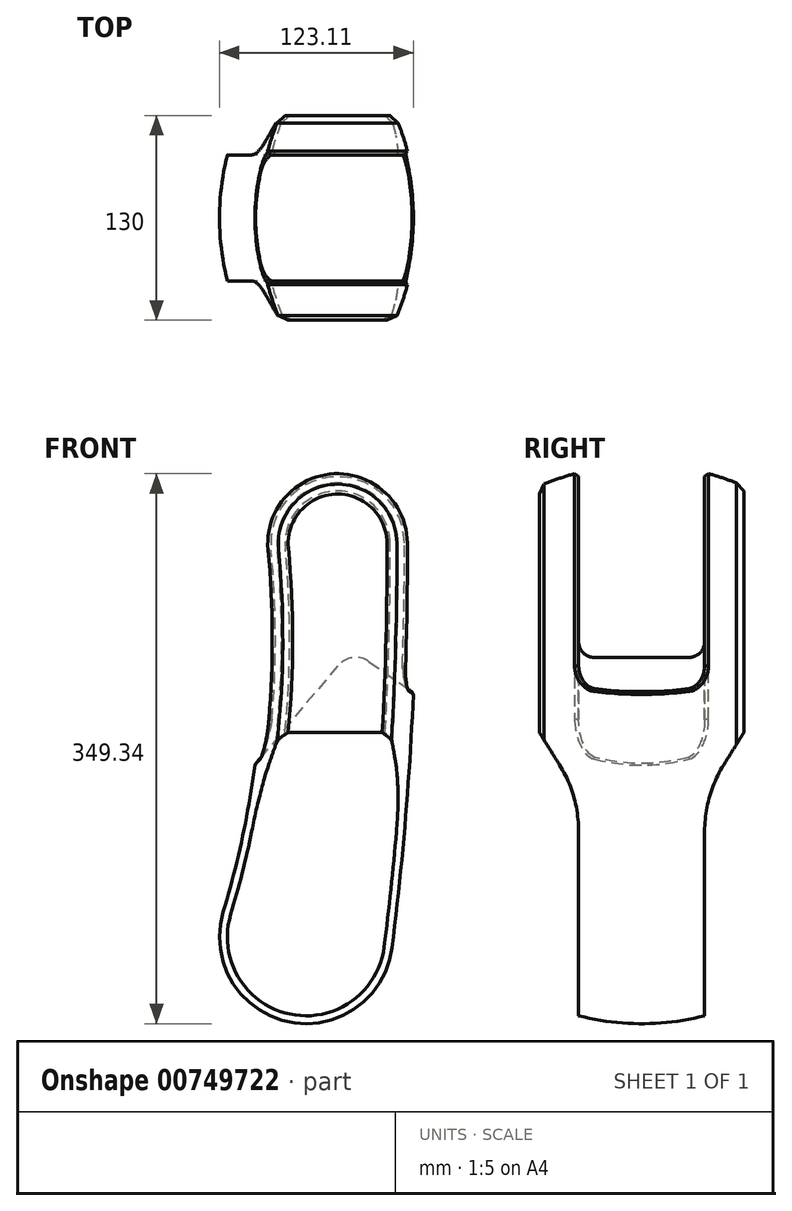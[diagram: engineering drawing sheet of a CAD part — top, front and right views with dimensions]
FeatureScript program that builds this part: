
annotation { "Feature Type Name" : "Feature", "Feature Type Description" : "" }
export const myFeature = defineFeature(function(context is Context, id is Id, definition is map)
    precondition{}
    {
        {
            var Q0;
            Q0=qCreatedBy(makeId("Front.planeOp"),FACE);
            var sketch = newSketch(context, id + "F0", { "sketchPlane" : qUnion([Q0])});
            skArc(sketch, "E0", {"start": v(50, 0.22) * mm, "mid": v(-2.46, 49.94) * mm, "end": v(-49.78, -4.7) * mm});
            skLineSegment(sketch, "E1", {"start": v(0, 0) * mm, "end": v(0, -250) * mm, "construction": true});
            skLineSegment(sketch, "E2", {"start": v(0, -250) * mm, "end": v(-20, -250) * mm, "construction": true});
            skArc(sketch, "E3", {"start": v(-72.66, -234.13) * mm, "mid": v(-31.39, -303.8) * mm, "end": v(34.58, -256.82) * mm});
            skArc(sketch, "E4", {"start": v(-72.66, -234.13) * mm, "mid": v(-50.1, -120.52) * mm, "end": v(-49.78, -4.7) * mm});
            skArc(sketch, "E5", {"start": v(34.58, -256.82) * mm, "mid": v(46.43, -128.55) * mm, "end": v(50, 0.22) * mm});
            skSolve(sketch);
        }
        {
            var Q0;
            Q0=qSketchRegion(id+"F0",true);
            extrude(context, id + "F1", {"entities" : qUnion([Q0]), "endBound" : BoundingType.SYMMETRIC, "depth" : 130 * mm, "offsetDistance" : 25 * mm});
        }
        {
            var Q0;
            Q0=qCreatedBy(makeId("Right.planeOp"),FACE);
            var sketch = newSketch(context, id + "F2", { "sketchPlane" : qUnion([Q0])});
            skLineSegment(sketch, "E6", {"start": v(0, 0) * mm, "end": v(0, -81.12) * mm, "construction": true});
            skLineSegment(sketch, "E7", {"start": v(0, 0) * mm, "end": v(0, 50) * mm, "construction": true});
            skArc(sketch, "E8", {"start": v(70, 34.15) * mm, "mid": v(0, 50) * mm, "end": v(-70, 34.15) * mm});
            skLineSegment(sketch, "E9", {"start": v(0, 50) * mm, "end": v(0, 72.15) * mm, "construction": true});
            skLineSegment(sketch, "E10", {"start": v(0, 72.15) * mm, "end": v(-70, 72.15) * mm});
            skLineSegment(sketch, "E11", {"start": v(-70, 72.15) * mm, "end": v(-70, 34.15) * mm});
            skLineSegment(sketch, "E12", {"start": v(-40, 72.15) * mm, "end": v(-40, 45) * mm, "construction": true});
            skLineSegment(sketch, "E13.MirrorCS", {"start": v(0, 72.15) * mm, "end": v(70, 72.15) * mm});
            skLineSegment(sketch, "E14.MirrorCS", {"start": v(70, 72.15) * mm, "end": v(70, 34.15) * mm});
            skLineSegment(sketch, "E15.MirrorCS", {"start": v(40, 72.15) * mm, "end": v(40, 45) * mm, "construction": true});
            skSolve(sketch);
        }
        {
            var Q0;
            Q0 = qSketchRegion(id + "F2", true);
            var Q1;
            Q1=makeQuery(id+"F1.opExtrude","CAP_EDGE",EDGE,{"disambiguationData":[OSD([sQuery(id+"F0.wireOp",EDGE,"E0")])],"isStart":true});
            var Q2;
            Q2=makeQuery(id+"F1.opExtrude","CAP_EDGE",EDGE,{"disambiguationData":[OSD([sQuery(id+"F0.wireOp",EDGE,"E5")])],"isStart":true});
            var Q3;
            Q3=makeQuery(id+"F1.opExtrude","CAP_EDGE",EDGE,{"disambiguationData":[OSD([sQuery(id+"F0.wireOp",EDGE,"E3")])],"isStart":true});
            var Q4;
            Q4=makeQuery(id+"F1.opExtrude","CAP_EDGE",EDGE,{"disambiguationData":[OSD([sQuery(id+"F0.wireOp",EDGE,"E4")])],"isStart":true});
            sweep(context, id + "F3", {"operationType" : NewBodyOperationType.REMOVE, "profiles" : qUnion([Q0]), "path" : qUnion([Q1, Q2, Q3, Q4])});
        }
        {
            var Q0;
            Q0=qCreatedBy(makeId("Front.planeOp"),FACE);
            var sketch = newSketch(context, id + "F4", { "sketchPlane" : qUnion([Q0])});
            skCircle(sketch, "E16", {"center": v(0, 0) * mm, "radius": 50 * mm, "construction": true});
            skLineSegment(sketch, "E17", {"start": v(0, 0) * mm, "end": v(0, -50) * mm, "construction": true});
            skLineSegment(sketch, "E18", {"start": v(8.85, -67.24) * mm, "end": v(-60.75, -150.19) * mm});
            skLineSegment(sketch, "E19", {"start": v(8.85, -67.24) * mm, "end": v(97.92, -129.6) * mm});
            skLineSegment(sketch, "E20", {"start": v(-60.75, -150.19) * mm, "end": v(-60.75, 51.2) * mm});
            skLineSegment(sketch, "E21", {"start": v(-60.75, 51.2) * mm, "end": v(97.92, 51.2) * mm});
            skLineSegment(sketch, "E22", {"start": v(97.92, 51.2) * mm, "end": v(97.92, -129.6) * mm});
            skSolve(sketch);
        }
        {
            var Q0;
            Q0=qSketchRegion(id+"F4",true);
            extrude(context, id + "F5", {"entities" : qUnion([Q0]), "operationType" : NewBodyOperationType.REMOVE, "endBound" : BoundingType.SYMMETRIC, "oppositeDirection" : true, "depth" : 80 * mm, "offsetDistance" : 25 * mm});
        }
        {
            var Q0;
            Q0=makeQuery(id+"F5.boolean.opBoolean","COPY",EDGE,{"derivedFrom":makeQuery(id+"F5.opExtrude","SWEPT_EDGE",EDGE,{"disambiguationData":[OSD([sQuery(id+"F4.wireOp",EDGE,"E18"),sQuery(id+"F4.wireOp",EDGE,"E19")])]})});
            fillet(context, id + "F6", {"entities" : qUnion([Q0]), "radius" : 15 * mm, "tangentPropagation" : true, "allowEdgeOverflow" : false});
        }
        {
            var Q0;
            Q0=makeQuery(id+"F5.boolean.opBoolean","COPY",EDGE,{"derivedFrom":makeQuery(id+"F5.opExtrude","CAP_EDGE",EDGE,{"disambiguationData":[OSD([sQuery(id+"F4.wireOp",EDGE,"E18")])],"isStart":false})});
            var Q1;
            Q1=makeQuery(id+"F5.boolean.opBoolean","COPY",EDGE,{"derivedFrom":makeQuery(id+"F5.opExtrude","CAP_EDGE",EDGE,{"disambiguationData":[OSD([sQuery(id+"F4.wireOp",EDGE,"E18")])],"isStart":true})});
            fillet(context, id + "F7", {"entities" : qUnion([Q0, Q1]), "radius" : 10 * mm, "tangentPropagation" : true, "allowEdgeOverflow" : false});
        }
        {
            var Q0;
            Q0=makeQuery(id+"F5.boolean.opBoolean","INTERSECT",EDGE,{"derivedFrom":[makeQuery(id+"F3.boolean.opBoolean","COPY",FACE,{"derivedFrom":makeQuery(id+"F3.opSweep","SWEPT_FACE",FACE,{"disambiguationData":[OSD([sQuery(id+"F0.wireOp",EDGE,"E0"),sQuery(id+"F2.wireOp",EDGE,"E8")])]})}),makeQuery(id+"F5.opExtrude","CAP_FACE",FACE,{"disambiguationData":[OSD([sQuery(id+"F4.wireOp",EDGE,"E18"),sQuery(id+"F4.wireOp",EDGE,"E19"),sQuery(id+"F4.wireOp",EDGE,"E20"),sQuery(id+"F4.wireOp",EDGE,"E21"),sQuery(id+"F4.wireOp",EDGE,"E22")])],"isStart":false})]});
            chamfer(context, id + "F8", {"entities" : qUnion([Q0]), "width" : 2 * mm, "tangentPropagation" : true});
        }
        {
            var Q0;
            Q0=qCreatedBy(makeId("Right.planeOp"),FACE);
            var sketch = newSketch(context, id + "F9", { "sketchPlane" : qUnion([Q0])});
            skLineSegment(sketch, "E23", {"start": v(0, 0) * mm, "end": v(0, -320) * mm, "construction": true});
            skLineSegment(sketch, "E24", {"start": v(0, -320) * mm, "end": v(40, -320) * mm, "construction": true});
            skLineSegment(sketch, "E25", {"start": v(40, -320) * mm, "end": v(40, -160) * mm});
            skLineSegment(sketch, "E26", {"start": v(40, -160) * mm, "end": v(65, -120) * mm});
            skLineSegment(sketch, "E27", {"start": v(65, -120) * mm, "end": v(65, -320) * mm});
            skLineSegment(sketch, "E28", {"start": v(65, -320) * mm, "end": v(40, -320) * mm});
            skLineSegment(sketch, "E29.MirrorCS", {"start": v(-40, -160) * mm, "end": v(-65, -120) * mm});
            skLineSegment(sketch, "E30.MirrorCS", {"start": v(-65, -320) * mm, "end": v(-40, -320) * mm});
            skLineSegment(sketch, "E31.MirrorCS", {"start": v(-40, -320) * mm, "end": v(-40, -160) * mm});
            skLineSegment(sketch, "E32.MirrorCS", {"start": v(-65, -120) * mm, "end": v(-65, -320) * mm});
            skSolve(sketch);
        }
        {
            var Q0;
            Q0 = qSketchRegion(id + "F9", true);
            extrude(context, id + "F10", {"entities" : qUnion([Q0]), "operationType" : NewBodyOperationType.REMOVE, "endBound" : BoundingType.THROUGH_ALL, "oppositeDirection" : true, "depth" : 25 * mm, "offsetDistance" : 25 * mm, "hasSecondDirection" : true, "secondDirectionBound" : SecondDirectionBoundingType.THROUGH_ALL, "secondDirectionOppositeDirection" : false, "secondDirectionDepth" : 25 * mm});
        }
        {
            var Q0;
            Q0=makeQuery(id+"F10.boolean.opBoolean","COPY",EDGE,{"derivedFrom":makeQuery(id+"F10.opExtrude","SWEPT_EDGE",EDGE,{"disambiguationData":[OSD([sQuery(id+"F9.wireOp",EDGE,"E26"),sQuery(id+"F9.wireOp",EDGE,"E27")])]})});
            var Q1;
            Q1=makeQuery(id+"F10.boolean.opBoolean","COPY",EDGE,{"derivedFrom":makeQuery(id+"F10.opExtrude","SWEPT_EDGE",EDGE,{"disambiguationData":[OSD([sQuery(id+"F9.wireOp",EDGE,"E25"),sQuery(id+"F9.wireOp",EDGE,"E26")])]})});
            var Q2;
            Q2=makeQuery(id+"F10.boolean.opBoolean","COPY",EDGE,{"derivedFrom":makeQuery(id+"F10.opExtrude","SWEPT_EDGE",EDGE,{"disambiguationData":[OSD([sQuery(id+"F9.wireOp",EDGE,"E29.MirrorCS"),sQuery(id+"F9.wireOp",EDGE,"E32.MirrorCS")])]})});
            var Q3;
            Q3=makeQuery(id+"F10.boolean.opBoolean","COPY",EDGE,{"derivedFrom":makeQuery(id+"F10.opExtrude","SWEPT_EDGE",EDGE,{"disambiguationData":[OSD([sQuery(id+"F9.wireOp",EDGE,"E29.MirrorCS"),sQuery(id+"F9.wireOp",EDGE,"E31.MirrorCS")])]})});
            fillet(context, id + "F11", {"entities" : qUnion([Q0, Q1, Q2, Q3]), "radius" : 80 * mm, "tangentPropagation" : true, "allowEdgeOverflow" : false});
        }
        {
            var Q0;
            {var subQ0=sQuery(id+"F0.wireOp",EDGE,"E0");Q0=makeQuery(id+"F3.boolean.opBoolean","INTERSECT",EDGE,{"derivedFrom":[makeQuery(id+"F1.opExtrude","CAP_FACE",FACE,{"disambiguationData":[OSD([subQ0,sQuery(id+"F0.wireOp",EDGE,"E3"),sQuery(id+"F0.wireOp",EDGE,"E4"),sQuery(id+"F0.wireOp",EDGE,"E5")])],"isStart":true}),makeQuery(id+"F3.opSweep","SWEPT_FACE",FACE,{"disambiguationData":[OSD([subQ0,sQuery(id+"F2.wireOp",EDGE,"E8")])]})]});}
            var Q1;
            {var subQ0=sQuery(id+"F0.wireOp",EDGE,"E0");Q1=makeQuery(id+"F3.boolean.opBoolean","INTERSECT",EDGE,{"derivedFrom":[makeQuery(id+"F1.opExtrude","CAP_FACE",FACE,{"disambiguationData":[OSD([subQ0,sQuery(id+"F0.wireOp",EDGE,"E3"),sQuery(id+"F0.wireOp",EDGE,"E4"),sQuery(id+"F0.wireOp",EDGE,"E5")])],"isStart":false}),makeQuery(id+"F3.opSweep","SWEPT_FACE",FACE,{"disambiguationData":[OSD([subQ0,sQuery(id+"F2.wireOp",EDGE,"E8")])]})]});}
            chamfer(context, id + "F12", {"entities" : qUnion([Q0, Q1]), "chamferType" : ChamferType.TWO_OFFSETS, "width1" : 3 * mm, "oppositeDirection" : false, "width2" : 5 * mm, "tangentPropagation" : true});
        }
    });
